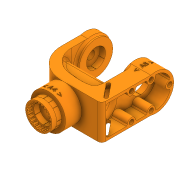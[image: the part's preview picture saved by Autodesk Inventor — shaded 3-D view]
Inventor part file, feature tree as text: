
AUTODESK INVENTOR PART (.ipt)
format: ipt  version: 2020 (Build 240168000, 168)  size: 2,166,784 bytes
history: native  units: in
note: dims shown in document units (in); Inventor stores cm internally (conversion verified against a paired STEP export)
features: sketch x42, extrude x38, projected_geometry x34, chamfer x8, fillet x8, plane x6, emboss x3
ambient origin geometry x8: Origin, YZ Plane, XZ Plane, XY Plane, X Axis, Y Axis, Z Axis, Center Point
bodies: Solid1 (feature_tree)
feature tree (139):
  extrude  "Extrusion1"  Depth=2.0472in
  extrude  "Extrusion2"  Depth=1.1063in
  chamfer  "Chamfer2"  Distance=0.2756in
  extrude  "Extrusion4"  Depth=0.0157in
  extrude  "Extrusion7"  Depth=0.2756in TaperAngle=0.0deg
  chamfer  "Chamfer4"  Distance=0.0394in
  extrude  "Extrusion8"  Depth=0.315in
  sketch  "Sketch12"  dims[d39=1.4567in d57=0.0394in d58=0.0in]
  plane  "Work Plane1"
  sketch  "Sketch13"  dims[d59=0.315in d60=0.125in d61=0.0137in d67=0.0157in]
  extrude  "Extrusion10"  Depth=0.0394in TaperAngle=0.0deg
  extrude  "Extrusion11"  Depth=0.0866in
  chamfer  "Chamfer5"  Distance=9.4488in Angle=360.0deg
  extrude  "Extrusion12"  Depth=0.2756in TaperAngle=0.0deg
  plane  "Work Plane2"
  extrude  "Extrusion13"  Depth=0.315in
  plane  "Work Plane3"
  extrude  "Extrusion14"  Depth=1.0236in
  extrude  "Extrusion15"  Depth=0.8858in
  extrude  "Extrusion16"  Depth=0.3937in
  extrude  "Extrusion17"  Depth=1.378in
  sketch  "Sketch21"  dims[d107=0.315in d108=0.0in d109=0.315in d110=0.125in d111=0.0137in]
  extrude  "Extrusion19"  Depth=0.5906in
  sketch  "Sketch23"  dims[d112=1.0in d113=0.0in d114=1.0236in]
  extrude  "Extrusion20"  Depth=0.1575in TaperAngle=0.0deg
  extrude  "Extrusion21"  Depth=0.1575in TaperAngle=0.0deg
  extrude  "Extrusion22"  Depth=4.2323in
  extrude  "Extrusion23"  Depth=0.1575in
  extrude  "Extrusion24"  Depth=1.1024in
  extrude  "Extrusion25"  Depth=0.4921in
  extrude  "Extrusion26"  Depth=0.75in
  extrude  "Extrusion27"  Depth=0.2165in TaperAngle=0.0deg
  extrude  "Extrusion28"  Depth=0.1575in
  extrude  "Extrusion29"  Depth=1.1811in
  plane  "Work Plane4"
  extrude  "Extrusion30"  Depth=0.315in TaperAngle=0.0deg
  fillet  "Fillet1"  Radius=0.3937in
  fillet  "Fillet2"  Radius=0.315in
  extrude  "Extrusion31"  Depth=0.315in TaperAngle=0.0deg
  extrude  "Extrusion32"  Depth=0.315in TaperAngle=0.0deg
  extrude  "Extrusion33"  Depth=0.3937in TaperAngle=0.0deg
  fillet  "Fillet3"  Radius=0.2165in
  extrude  "Extrusion34"  Depth=0.4724in
  chamfer  "Chamfer6"  Distance=0.2756in
  chamfer  "Chamfer7"  Distance=0.0394in
  extrude  "Extrusion35"  Depth=0.001in
  extrude  "Extrusion36"  Depth=1.0in TaperAngle=0.0deg
  fillet  "Fillet5"  Radius=0.1575in
  extrude  "Extrusion38"  Depth=0.315in
  extrude  "Extrusion39"  Depth=0.315in
  extrude  "Extrusion40"  Depth=0.1378in TaperAngle=0.0deg
  fillet  "Fillet7"  Radius=1.0in
  extrude  "Extrusion41"  Depth=0.1969in
  chamfer  "Chamfer8"  Distance=0.3937in
  extrude  "Extrusion42"  Depth=0.1378in
  plane  "Work Plane6"
  emboss  "Emboss1"
  emboss  "Emboss2"
  plane  "Work Plane7"
  emboss  "Emboss3"
  extrude  "Extrusion43"  Depth=0.1378in
  fillet  "Fillet9"  Radius=0.1969in
  fillet  "Fillet10"  Radius=0.1181in
  chamfer  "Chamfer9"  Distance=1.0039in
  fillet  "Fillet11"  Radius=0.4134in
  chamfer  "Chamfer10"  Distance=0.5118in
  extrude  "Extrusion44"  Depth=0.1378in
  sketch  "Sketch1"  dims[d0=0.6299in d1=2.0472in]
  sketch  "Sketch2"  dims[d2=0.9449in d3=0.0in d4=1.1063in]
  sketch  "Sketch4"  dims[d5=1.5748in d6=0.2756in d7=0.0in]
  sketch  "Sketch8"  dims[d11=0.2756in d12=0.125in d13=0.0137in d25=0.0157in]
  projected_geometry  "Projected Loop2"
  sketch  "Sketch10"  dims[d26=6.2992in d28=360.0deg d30=0.2756in d31=0.0in]
  sketch  "Sketch14"  dims[d68=4.7244in d70=360.0deg d72=0.0394in d73=0.0in]
  sketch  "Sketch15"  dims[d83=0.0591in d84=0.0866in]
  projected_geometry  "Projected Loop4"
  sketch  "Sketch16"  dims[d85=0.0827in]
  sketch  "Sketch17"  dims[d86=0.0827in]
  projected_geometry  "Projected Loop5"
  sketch  "Sketch18"  dims[d87=0.0827in d88=9.4488in d90=360.0deg]
  projected_geometry  "Projected Loop6"
  projected_geometry  "Projected Loop7"
  sketch  "Sketch19"  dims[d92=0.2756in]
  projected_geometry  "Projected Loop8"
  projected_geometry  "Projected Loop9"
  sketch  "Sketch20"  dims[d94=9.4488in d95=0.0827in d96=0.0827in d97=0.0827in d98=360.0deg d105=0.2756in d106=0.0in]
  projected_geometry  "Projected Loop10"
  projected_geometry  "Projected Loop11"
  projected_geometry  "Projected Loop12"
  projected_geometry  "Projected Loop13"
  sketch  "Sketch25"  dims[d115=0.7874in d117=0.8858in]
  sketch  "Sketch26"  dims[d118=2.7559in d119=0.3937in]
  projected_geometry  "Projected Loop16"
  projected_geometry  "Projected Loop17"
  sketch  "Sketch27"  dims[d120=0.5906in d121=1.378in]
  projected_geometry  "Projected Loop18"
  projected_geometry  "Projected Loop19"
  sketch  "Sketch28"  dims[d123=3.4941in d124=0.5906in]
  projected_geometry  "Projected Loop20"
  projected_geometry  "Projected Loop21"
  sketch  "Sketch29"  dims[d126=1.9685in d129=0.1575in d130=0.0in]
  projected_geometry  "Projected Loop22"
  projected_geometry  "Projected Loop23"
  sketch  "Sketch30"  dims[d131=-2.0472in d132=0.1575in d133=0.0in]
  projected_geometry  "Projected Loop24"
  sketch  "Sketch31"  dims[d134=2.126in d136=4.2323in]
  sketch  "Sketch32"  dims[d137=0.1575in d138=0.1575in]
  sketch  "Sketch34"  dims[d139=0.4921in d140=0.0in d141=1.1024in]
  projected_geometry  "Projected Loop25"
  sketch  "Sketch35"  dims[d142=1.1614in d143=0.4921in]
  sketch  "Sketch36"  dims[d144=0.3445in d145=0.75in]
  projected_geometry  "Projected Loop26"
  sketch  "Sketch37"  dims[d146=0.1575in d147=0.0in d148=0.2165in d149=0.0in]
  projected_geometry  "Projected Loop27"
  sketch  "Sketch38"  dims[d152=1.0039in d153=0.0in d154=0.1575in]
  projected_geometry  "Projected Loop28"
  sketch  "Sketch39"  dims[d155=0.1575in d160=1.1811in]
  projected_geometry  "Projected Loop29"
  sketch  "Sketch40"  dims[d161=0.1969in d162=0.0in d163=0.315in d164=0.0in d165=0.3937in d166=0.0in d167=0.315in d168=0.0in]
  sketch  "Sketch41"  dims[d169=0.315in d170=0.0in d171=0.315in d172=0.0in]
  projected_geometry  "Projected Loop30"
  sketch  "Sketch43"  dims[d173=0.315in d174=0.0in d175=0.315in d176=0.0in]
  projected_geometry  "Projected Loop31"
  sketch  "Sketch44"  dims[d177=1.1024in d178=0.3937in d179=0.0in d180=0.2165in d181=0.0in]
  sketch  "Sketch45"  dims[d183=-0.0197in d184=0.4724in d185=0.2756in d186=0.0in]
  sketch  "Sketch46"  dims[d187=0.5512in]
  projected_geometry  "Projected Loop32"
  sketch  "Sketch47"  dims[d188=0.2165in d189=0.0394in d190=0.0in]
  projected_geometry  "Projected Loop33"
  sketch  "Sketch48"  dims[d191=0.0394in d192=0.0in d193=0.001in]
  sketch  "Sketch49"  dims[d194=0.001in d195=1.0in d196=0.0in d197=0.1575in]
  sketch  "Sketch50"  dims[d198=1.0in d199=0.0in d200=0.315in d201=0.125in d202=0.0137in]
  sketch  "Sketch52"  dims[d203=0.315in d204=0.125in d205=0.0137in d206=0.0157in]
  sketch  "Sketch53"  dims[d207=2.3622in d209=360.0deg d211=1.0in d212=0.0in d213=1.0in d214=0.0in d221=0.1969in d222=0.3937in d223=0.0in d224=0.1575in d225=0.0787in d226=0.1969in d227=0.0in d229=0.1181in d230=1.0039in d231=0.4134in d232=0.5118in d233=0.0984in d235=0.0197in d236=0.1181in d237=0.1181in d238=0.2047in d239=0.2047in d240=0.0in d241=0.0in d242=0.2362in d243=0.0787in d244=0.0787in d251=0.0787in d252=0.0787in d253=0.2756in d254=0.4724in d255=0.2756in d256=0.4724in d257=0.2756in d258=0.4724in d259=0.2756in d260=0.4724in d261=0.1575in d262=0.0in d263=0.0787in d264=0.125in d265=45.0deg d266=1.0in d267=0.0in d269=0.0394in d270=0.0in d271=0.0394in d272=0.0in d273=0.0394in d274=0.0in d275=0.0039in d276=0.0787in d277=1.0in d278=0.0in d279=0.122in d280=0.2361in d282=0.1378in d283=0.2047in d284=0.1575in d285=0.125in d286=45.0deg d287=0.1575in d288=0.0394in d289=0.125in d290=45.0deg d291=0.5709in d292=0.0in]
  projected_geometry  "Projected Loop35"
  projected_geometry  "Projected Loop36"
  projected_geometry  "Projected Loop37"
  projected_geometry  "Projected Loop38"
  projected_geometry  "Projected Loop39"
